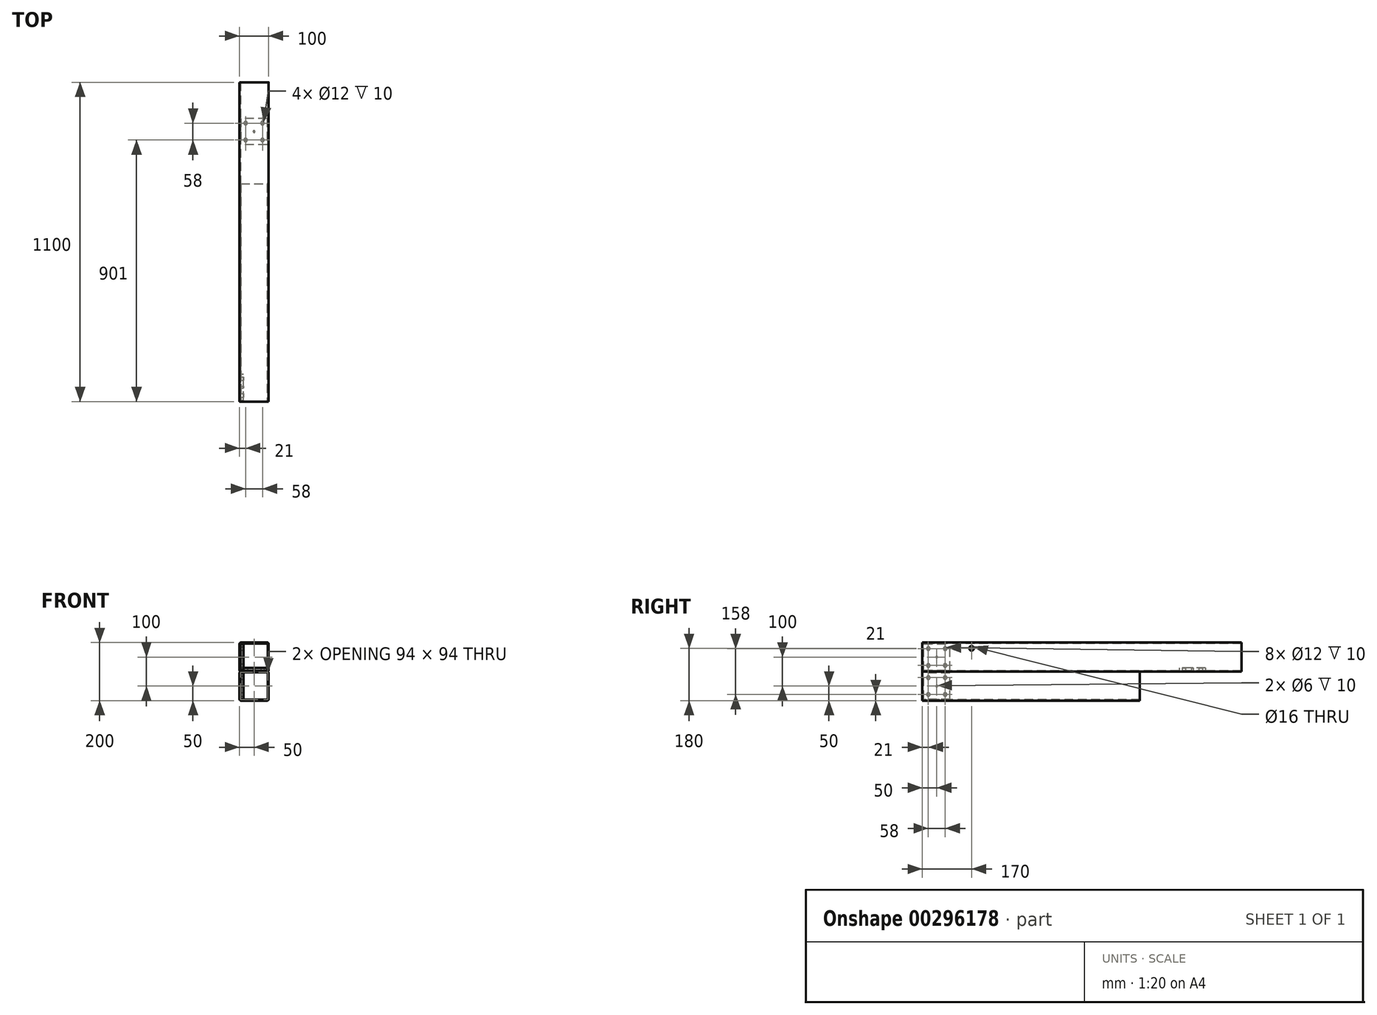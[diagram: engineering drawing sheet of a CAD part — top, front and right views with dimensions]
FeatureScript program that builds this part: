
annotation { "Feature Type Name" : "Feature", "Feature Type Description" : "" }
export const myFeature = defineFeature(function(context is Context, id is Id, definition is map)
    precondition{}
    {
        {
            var Q0;
            Q0=qCreatedBy(makeId("Front.planeOp"),FACE);
            var sketch = newSketch(context, id + "F0", { "sketchPlane" : qUnion([Q0])});
            skLineSegment(sketch, "E0.bottom", {"start": v(45, 50) * mm, "end": v(-45, 50) * mm});
            skLineSegment(sketch, "E0.top", {"start": v(45, -50) * mm, "end": v(-45, -50) * mm});
            skLineSegment(sketch, "E0.left", {"start": v(50, 45) * mm, "end": v(50, -45) * mm});
            skLineSegment(sketch, "E0.right", {"start": v(-50, 45) * mm, "end": v(-50, -45) * mm});
            skPoint(sketch, "E0.middle", {"position": v(0, 0) * mm});
            skPoint(sketch, "E1.visualSharp", {"position": v(-50, 50) * mm});
            skArc(sketch, "E1.filletArc", {"start": v(-45, 50) * mm, "mid": v(-48.54, 48.54) * mm, "end": v(-50, 45) * mm});
            skPoint(sketch, "E2.visualSharp", {"position": v(50, 50) * mm});
            skArc(sketch, "E2.filletArc", {"start": v(50, 45) * mm, "mid": v(48.54, 48.54) * mm, "end": v(45, 50) * mm});
            skPoint(sketch, "E3.visualSharp", {"position": v(50, -50) * mm});
            skArc(sketch, "E3.filletArc", {"start": v(45, -50) * mm, "mid": v(48.54, -48.54) * mm, "end": v(50, -45) * mm});
            skPoint(sketch, "E4.visualSharp", {"position": v(-50, -50) * mm});
            skArc(sketch, "E4.filletArc", {"start": v(-50, -45) * mm, "mid": v(-48.54, -48.54) * mm, "end": v(-45, -50) * mm});
            skArc(sketch, "E5.0", {"start": v(-45, 47) * mm, "mid": v(-46.41, 46.41) * mm, "end": v(-47, 45) * mm});
            skLineSegment(sketch, "E5.1", {"start": v(45, 47) * mm, "end": v(-45, 47) * mm});
            skLineSegment(sketch, "E5.2", {"start": v(-47, 45) * mm, "end": v(-47, -45) * mm});
            skArc(sketch, "E5.3", {"start": v(47, 45) * mm, "mid": v(46.41, 46.41) * mm, "end": v(45, 47) * mm});
            skArc(sketch, "E5.4", {"start": v(-47, -45) * mm, "mid": v(-46.41, -46.41) * mm, "end": v(-45, -47) * mm});
            skLineSegment(sketch, "E5.5", {"start": v(45, -47) * mm, "end": v(-45, -47) * mm});
            skArc(sketch, "E5.6", {"start": v(45, -47) * mm, "mid": v(46.41, -46.41) * mm, "end": v(47, -45) * mm});
            skLineSegment(sketch, "E5.7", {"start": v(47, 45) * mm, "end": v(47, -45) * mm});
            skLineSegment(sketch, "E6.top", {"start": v(45, -150) * mm, "end": v(-45, -150) * mm});
            skLineSegment(sketch, "E6.left", {"start": v(50, -55) * mm, "end": v(50, -145) * mm});
            skLineSegment(sketch, "E6.right", {"start": v(-50, -55) * mm, "end": v(-50, -145) * mm});
            skPoint(sketch, "E6.middle", {"position": v(0, -100) * mm});
            skArc(sketch, "E7.filletArc", {"start": v(-45, -50) * mm, "mid": v(-48.54, -51.46) * mm, "end": v(-50, -55) * mm});
            skArc(sketch, "E8.filletArc", {"start": v(50, -55) * mm, "mid": v(48.54, -51.46) * mm, "end": v(45, -50) * mm});
            skPoint(sketch, "E9.visualSharp", {"position": v(50, -150) * mm});
            skArc(sketch, "E9.filletArc", {"start": v(45, -150) * mm, "mid": v(48.54, -148.54) * mm, "end": v(50, -145) * mm});
            skPoint(sketch, "E10.visualSharp", {"position": v(-50, -150) * mm});
            skArc(sketch, "E10.filletArc", {"start": v(-50, -145) * mm, "mid": v(-48.54, -148.54) * mm, "end": v(-45, -150) * mm});
            skArc(sketch, "E11.0", {"start": v(-45, -53) * mm, "mid": v(-46.41, -53.59) * mm, "end": v(-47, -55) * mm});
            skLineSegment(sketch, "E11.1", {"start": v(45, -53) * mm, "end": v(-45, -53) * mm});
            skLineSegment(sketch, "E11.2", {"start": v(-47, -55) * mm, "end": v(-47, -145) * mm});
            skArc(sketch, "E11.3", {"start": v(47, -55) * mm, "mid": v(46.41, -53.59) * mm, "end": v(45, -53) * mm});
            skArc(sketch, "E11.4", {"start": v(-47, -145) * mm, "mid": v(-46.41, -146.41) * mm, "end": v(-45, -147) * mm});
            skLineSegment(sketch, "E11.5", {"start": v(45, -147) * mm, "end": v(-45, -147) * mm});
            skArc(sketch, "E11.6", {"start": v(45, -147) * mm, "mid": v(46.41, -146.41) * mm, "end": v(47, -145) * mm});
            skLineSegment(sketch, "E11.7", {"start": v(47, -55) * mm, "end": v(47, -145) * mm});
            skSolve(sketch);
        }
        {
            var Q0;
            Q0=makeQuery(id+"F0.imprint","IMPRINT",FACE,{"disambiguationData":[TD([[makeQuery(id+"F0.imprint","IMPRINT",EDGE,{"derivedFrom":sQuery(id+"F0.wireOp",EDGE,"E0.bottom")}),1.0]])]});
            var Q1;
            Q1=makeQuery(id+"F0.imprint","IMPRINT",FACE,{"disambiguationData":[TD([[makeQuery(id+"F0.imprint","IMPRINT",EDGE,{"derivedFrom":sQuery(id+"F0.wireOp",EDGE,"E0.top")}),1.0]])]});
            extrude(context, id + "F1", {"entities" : qUnion([Q0, Q1]), "oppositeDirection" : true, "depth" : 1100 * mm});
        }
        {
            var Q0;
            Q0=makeQuery(id+"F1.opExtrude","SWEPT_FACE",FACE,{"disambiguationData":[OSD([sQuery(id+"F0.wireOp",EDGE,"E0.left")])]});
            var sketch = newSketch(context, id + "F2", { "sketchPlane" : qUnion([Q0])});
            skCircle(sketch, "E12", {"center": v(170, 30) * mm, "radius": 8 * mm});
            skSolve(sketch);
        }
        {
            var Q0;
            Q0=makeQuery(id+"F2.imprint","IMPRINT",FACE,{"disambiguationData":[TD([[makeQuery(id+"F2.imprint","IMPRINT",EDGE,{"derivedFrom":sQuery(id+"F2.wireOp",EDGE,"E12")}),1.0]])]});
            extrude(context, id + "F3", {"entities" : qUnion([Q0]), "operationType" : NewBodyOperationType.REMOVE, "endBound" : BoundingType.UP_TO_NEXT, "oppositeDirection" : true, "depth" : 25 * mm});
        }
        {
            var Q0;
            Q0=makeQuery(id+"F1.opExtrude","SWEPT_FACE",FACE,{"disambiguationData":[OSD([sQuery(id+"F0.wireOp",EDGE,"E6.left")])]});
            var sketch = newSketch(context, id + "F4", { "sketchPlane" : qUnion([Q0])});
            skLineSegment(sketch, "E13.bottom", {"start": v(750, -50) * mm, "end": v(1100, -50) * mm});
            skLineSegment(sketch, "E13.top", {"start": v(750, -150) * mm, "end": v(1100, -150) * mm});
            skLineSegment(sketch, "E13.left", {"start": v(750, -50) * mm, "end": v(750, -150) * mm});
            skLineSegment(sketch, "E13.right", {"start": v(1100, -50) * mm, "end": v(1100, -150) * mm});
            skSolve(sketch);
        }
        {
            var Q0;
            {var subQ0=sQuery(id+"F4.wireOp",EDGE,"E13.left");var subQ1=sQuery(id+"F0.wireOp",EDGE,"E6.left");var subQ2=makeQuery(id+"F1.opExtrude","SWEPT_EDGE",EDGE,{"disambiguationData":[OSD([subQ1,sQuery(id+"F0.wireOp",EDGE,"E8.filletArc")])]});var subQ3=makeQuery(id+"F4.imprint","INTERSECT",VERTEX,{"derivedFrom":[subQ2,subQ0]});Q0=makeQuery(id+"F4.imprint","IMPRINT",FACE,{"disambiguationData":[TD([[makeQuery(id+"F4.imprint","IMPRINT",EDGE,{"disambiguationData":[TD([[subQ3,-1.0]])],"derivedFrom":subQ0}),1.0]])]});}
            var Q1;
            {var subQ0=sQuery(id+"F4.wireOp",EDGE,"E13.top");Q1=makeQuery(id+"F4.imprint","IMPRINT",FACE,{"disambiguationData":[TD([[makeQuery(id+"F4.imprint","IMPRINT",EDGE,{"derivedFrom":subQ0}),1.0]])]});}
            var Q2;
            {var subQ0=sQuery(id+"F4.wireOp",EDGE,"E13.bottom");Q2=makeQuery(id+"F4.imprint","IMPRINT",FACE,{"disambiguationData":[TD([[makeQuery(id+"F4.imprint","IMPRINT",EDGE,{"derivedFrom":subQ0}),-1.0]])]});}
            extrude(context, id + "F5", {"entities" : qUnion([Q0, Q1, Q2]), "operationType" : NewBodyOperationType.REMOVE, "endBound" : BoundingType.THROUGH_ALL, "oppositeDirection" : true, "depth" : 25 * mm});
        }
        {
            var Q0;
            Q0=makeQuery(id+"F1.opExtrude","SWEPT_FACE",FACE,{"disambiguationData":[OSD([sQuery(id+"F0.wireOp",EDGE,"E6.left")])]});
            var sketch = newSketch(context, id + "F6", { "sketchPlane" : qUnion([Q0])});
            skLineSegment(sketch, "E14.bottom", {"start": v(5, -45) * mm, "end": v(95, -45) * mm});
            skLineSegment(sketch, "E14.top", {"start": v(5, 45) * mm, "end": v(95, 45) * mm});
            skLineSegment(sketch, "E14.left", {"start": v(5, -45) * mm, "end": v(5, 45) * mm});
            skLineSegment(sketch, "E14.right", {"start": v(95, -45) * mm, "end": v(95, 45) * mm});
            skPoint(sketch, "E14.middle", {"position": v(50, 0) * mm});
            skLineSegment(sketch, "E15", {"start": v(95, 45) * mm, "end": v(5, -45) * mm, "construction": true});
            skLineSegment(sketch, "E16", {"start": v(5, 45) * mm, "end": v(95, -45) * mm, "construction": true});
            skLineSegment(sketch, "E17", {"start": v(95, -29) * mm, "end": v(5, -29) * mm, "construction": true});
            skCircle(sketch, "E18", {"center": v(21, -29) * mm, "radius": 6 * mm});
            skCircle(sketch, "E19", {"center": v(79, -29) * mm, "radius": 6 * mm});
            skLineSegment(sketch, "E20", {"start": v(79, -29) * mm, "end": v(79, 29) * mm, "construction": true});
            skLineSegment(sketch, "E21", {"start": v(79, 29) * mm, "end": v(21, 29) * mm, "construction": true});
            skCircle(sketch, "E22", {"center": v(21, 29) * mm, "radius": 6 * mm});
            skCircle(sketch, "E23", {"center": v(79, 29) * mm, "radius": 6 * mm});
            skLineSegment(sketch, "E24.bottom", {"start": v(5, -145) * mm, "end": v(95, -145) * mm});
            skLineSegment(sketch, "E24.top", {"start": v(5, -55) * mm, "end": v(95, -55) * mm});
            skLineSegment(sketch, "E24.left", {"start": v(5, -145) * mm, "end": v(5, -55) * mm});
            skLineSegment(sketch, "E24.right", {"start": v(95, -145) * mm, "end": v(95, -55) * mm});
            skPoint(sketch, "E24.middle", {"position": v(50, -100) * mm});
            skLineSegment(sketch, "E25", {"start": v(95, -55) * mm, "end": v(5, -145) * mm, "construction": true});
            skLineSegment(sketch, "E26", {"start": v(5, -55) * mm, "end": v(95, -145) * mm, "construction": true});
            skLineSegment(sketch, "E27", {"start": v(95, -129) * mm, "end": v(5, -129) * mm, "construction": true});
            skCircle(sketch, "E28", {"center": v(21, -129) * mm, "radius": 6 * mm});
            skCircle(sketch, "E29", {"center": v(79, -129) * mm, "radius": 6 * mm});
            skLineSegment(sketch, "E30", {"start": v(79, -129) * mm, "end": v(79, -71) * mm, "construction": true});
            skLineSegment(sketch, "E31", {"start": v(79, -71) * mm, "end": v(21, -71) * mm, "construction": true});
            skCircle(sketch, "E32", {"center": v(21, -71) * mm, "radius": 6 * mm});
            skCircle(sketch, "E33", {"center": v(79, -71) * mm, "radius": 6 * mm});
            skCircle(sketch, "E34", {"center": v(50, -100) * mm, "radius": 3 * mm});
            skCircle(sketch, "E35", {"center": v(50, 0) * mm, "radius": 3 * mm});
            skSolve(sketch);
        }
        {
            var Q0;
            Q0 = qSketchRegion(id + "F6", true);
            extrude(context, id + "F7", {"entities" : qUnion([Q0]), "operationType" : NewBodyOperationType.ADD, "oppositeDirection" : true, "depth" : (100 - 3) * mm, "hasSecondDirection" : true, "secondDirectionOppositeDirection" : true, "secondDirectionDepth" : (100 - 3 - 10) * mm});
        }
        {
            var Q0;
            Q0=makeQuery(id+"F5.boolean.opBoolean","COPY",FACE,{"derivedFrom":makeQuery(id+"F5.opExtrude","SWEPT_FACE",FACE,{"disambiguationData":[OSD([sQuery(id+"F4.wireOp",EDGE,"E13.bottom")])]})});
            var sketch = newSketch(context, id + "F8", { "sketchPlane" : qUnion([Q0])});
            skLineSegment(sketch, "E36.bottom", {"start": v(-45, -975) * mm, "end": v(45, -975) * mm});
            skLineSegment(sketch, "E36.top", {"start": v(-45, -885) * mm, "end": v(45, -885) * mm});
            skLineSegment(sketch, "E36.left", {"start": v(-45, -975) * mm, "end": v(-45, -885) * mm});
            skLineSegment(sketch, "E36.right", {"start": v(45, -975) * mm, "end": v(45, -885) * mm});
            skPoint(sketch, "E36.middle", {"position": v(0, -930) * mm});
            skLineSegment(sketch, "E37", {"start": v(45, -885) * mm, "end": v(-45, -975) * mm, "construction": true});
            skLineSegment(sketch, "E38", {"start": v(-45, -885) * mm, "end": v(45, -975) * mm, "construction": true});
            skLineSegment(sketch, "E39", {"start": v(45, -959) * mm, "end": v(-45, -959) * mm, "construction": true});
            skCircle(sketch, "E40", {"center": v(-29, -959) * mm, "radius": 6 * mm});
            skCircle(sketch, "E41", {"center": v(29, -959) * mm, "radius": 6 * mm});
            skLineSegment(sketch, "E42", {"start": v(29, -959) * mm, "end": v(29, -901) * mm, "construction": true});
            skLineSegment(sketch, "E43", {"start": v(29, -901) * mm, "end": v(-29, -901) * mm, "construction": true});
            skCircle(sketch, "E44", {"center": v(-29, -901) * mm, "radius": 6 * mm});
            skCircle(sketch, "E45", {"center": v(29, -901) * mm, "radius": 6 * mm});
            skCircle(sketch, "E46", {"center": v(0, -930) * mm, "radius": 3 * mm});
            skSolve(sketch);
        }
        {
            var Q0;
            Q0=makeQuery(id+"F8.imprint","IMPRINT",FACE,{"disambiguationData":[TD([[makeQuery(id+"F8.imprint","IMPRINT",EDGE,{"derivedFrom":sQuery(id+"F8.wireOp",EDGE,"E36.bottom")}),1.0]])]});
            extrude(context, id + "F9", {"entities" : qUnion([Q0]), "operationType" : NewBodyOperationType.ADD, "oppositeDirection" : true, "depth" : 13 * mm});
        }
    });
